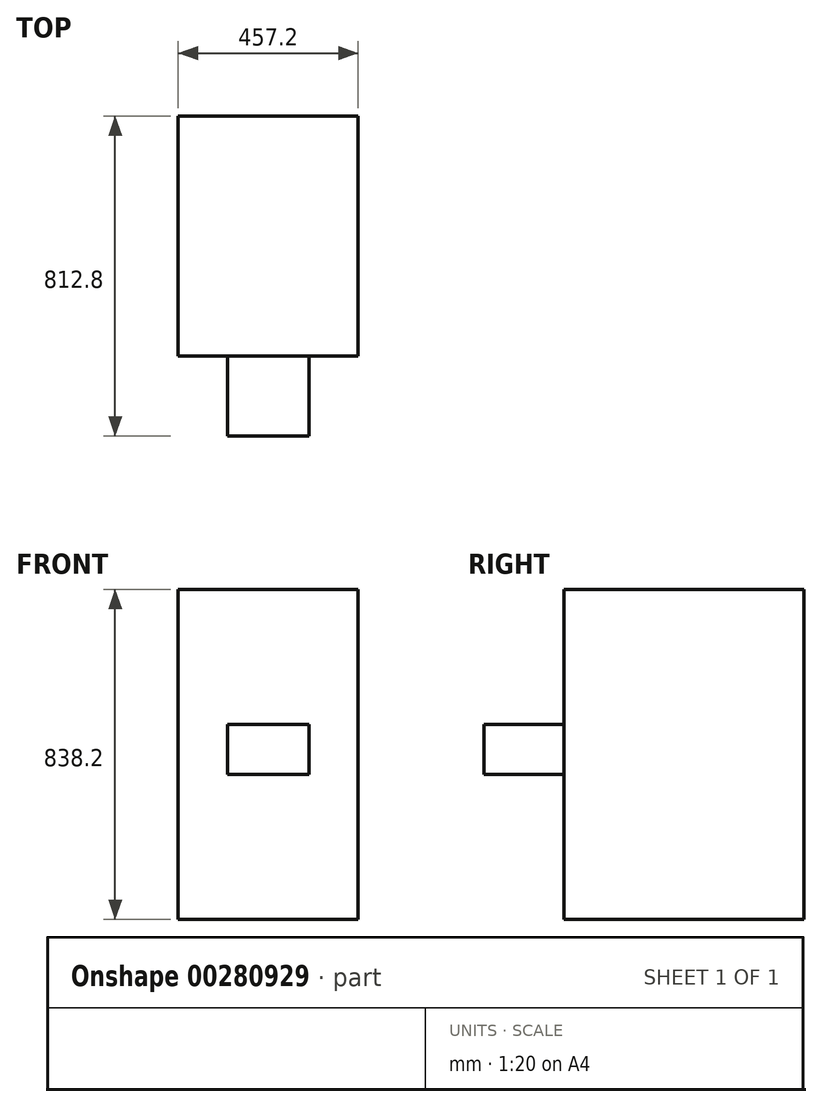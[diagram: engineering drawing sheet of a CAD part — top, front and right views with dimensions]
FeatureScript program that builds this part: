
annotation { "Feature Type Name" : "Feature", "Feature Type Description" : "" }
export const myFeature = defineFeature(function(context is Context, id is Id, definition is map)
    precondition{}
    {
        {
            var Q0;
            Q0=qCreatedBy(makeId("Top.planeOp"),FACE);
            var sketch = newSketch(context, id + "F0", { "sketchPlane" : qUnion([Q0])});
            skLineSegment(sketch, "E0.bottom", {"start": v(0, 0) * mm, "end": v(457.2, 0) * mm});
            skLineSegment(sketch, "E0.top", {"start": v(0, 609.6) * mm, "end": v(457.2, 609.6) * mm});
            skLineSegment(sketch, "E0.left", {"start": v(0, 0) * mm, "end": v(0, 609.6) * mm});
            skLineSegment(sketch, "E0.right", {"start": v(457.2, 0) * mm, "end": v(457.2, 609.6) * mm});
            skSolve(sketch);
        }
        {
            var Q0;
            Q0=makeQuery(id+"F0.imprint","IMPRINT",FACE,{"disambiguationData":[TD([[makeQuery(id+"F0.imprint","IMPRINT",EDGE,{"derivedFrom":sQuery(id+"F0.wireOp",EDGE,"E0.bottom")}),1.0]])]});
            extrude(context, id + "F1", {"entities" : qUnion([Q0]), "depth" : 838.2 * mm, "offsetDistance" : 25.4 * mm});
        }
        {
            var Q0;
            Q0=makeQuery(id+"F1.opExtrude","SWEPT_FACE",FACE,{"disambiguationData":[OSD([sQuery(id+"F0.wireOp",EDGE,"E0.bottom")])]});
            var sketch = newSketch(context, id + "F2", { "sketchPlane" : qUnion([Q0])});
            skLineSegment(sketch, "E1", {"start": v(0, 838.2) * mm, "end": v(0, 666.75) * mm, "construction": true});
            skLineSegment(sketch, "E2", {"start": v(0, 666.75) * mm, "end": v(0, 431.8) * mm, "construction": true});
            skLineSegment(sketch, "E3", {"start": v(228.6, 838.2) * mm, "end": v(228.6, 431.8) * mm, "construction": true});
            skLineSegment(sketch, "E4.bottom", {"start": v(331.98, 368.3) * mm, "end": v(125.22, 368.3) * mm});
            skLineSegment(sketch, "E4.top", {"start": v(331.98, 495.3) * mm, "end": v(125.22, 495.3) * mm});
            skLineSegment(sketch, "E4.left", {"start": v(331.98, 368.3) * mm, "end": v(331.98, 495.3) * mm});
            skLineSegment(sketch, "E4.right", {"start": v(125.22, 368.3) * mm, "end": v(125.22, 495.3) * mm});
            skPoint(sketch, "E4.middle", {"position": v(228.6, 431.8) * mm});
            skSolve(sketch);
        }
        {
            var Q0;
            Q0=makeQuery(id+"F2.imprint","IMPRINT",FACE,{"disambiguationData":[TD([[makeQuery(id+"F2.imprint","IMPRINT",EDGE,{"derivedFrom":sQuery(id+"F2.wireOp",EDGE,"E4.bottom")}),-1.0]])]});
            extrude(context, id + "F3", {"entities" : qUnion([Q0]), "operationType" : NewBodyOperationType.ADD, "depth" : 25.4 * mm, "offsetDistance" : 25.4 * mm});
        }
        {
            var Q0;
            Q0=makeQuery(id+"F3.opExtrude","CAP_FACE",FACE,{"disambiguationData":[OSD([sQuery(id+"F2.wireOp",EDGE,"E4.bottom"),sQuery(id+"F2.wireOp",EDGE,"E4.top"),sQuery(id+"F2.wireOp",EDGE,"E4.left"),sQuery(id+"F2.wireOp",EDGE,"E4.right")])],"isStart":false});
            extrude(context, id + "F4", {"entities" : qUnion([Q0]), "operationType" : NewBodyOperationType.ADD, "depth" : 177.8 * mm, "offsetDistance" : 25.4 * mm});
        }
    });
